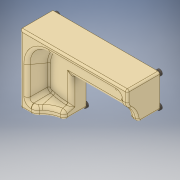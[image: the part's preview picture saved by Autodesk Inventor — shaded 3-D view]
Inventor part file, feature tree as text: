
AUTODESK INVENTOR PART (.ipt)
format: ipt  version: 2019 (Build 230136000, 136)  size: 566,784 bytes
history: native  units: mm
features: other x6, sketch x5, extrude x5, fillet x4, projected_geometry x4
ambient origin geometry x8: Origin, YZ Plane, XZ Plane, XY Plane, X Axis, Y Axis, Z Axis, Center Point
bodies: Body1 (feature_tree), Body2 (feature_tree)
feature tree (24):
  other  "Твердое тело1"
  sketch  "Эскиз1"
  other  "РабПлоскость1"
  other  "РабПлоскость2"
  extrude  "Выдавливание1"  Depth=2900.0mm
  other  "РабПлоскость3"
  extrude  "Выдавливание2"  Depth=900.0mm
  extrude  "Выдавливание3"  Depth=1850.0mm
  extrude  "Выдавливание4"  Depth=900.0mm
  other  "НаклГрань1"
  fillet  "Сопряжение1"  Radius=50.0mm
  fillet  "Сопряжение2"  Radius=10.0mm
  fillet  "Сопряжение3"  Radius=930.0mm
  fillet  "Сопряжение4"  Radius=300.0mm
  extrude  "Выдавливание5"  Depth=300.0mm
  sketch  "Эскиз2"
  projected_geometry  "Спроецированная петля1"
  sketch  "Эскиз3"
  projected_geometry  "Спроецированная петля2"
  sketch  "Эскиз4"
  projected_geometry  "Спроецированная петля3"
  sketch  "Эскиз5"
  projected_geometry  "Спроецированная петля4"
  other  "Твердое тело2"
